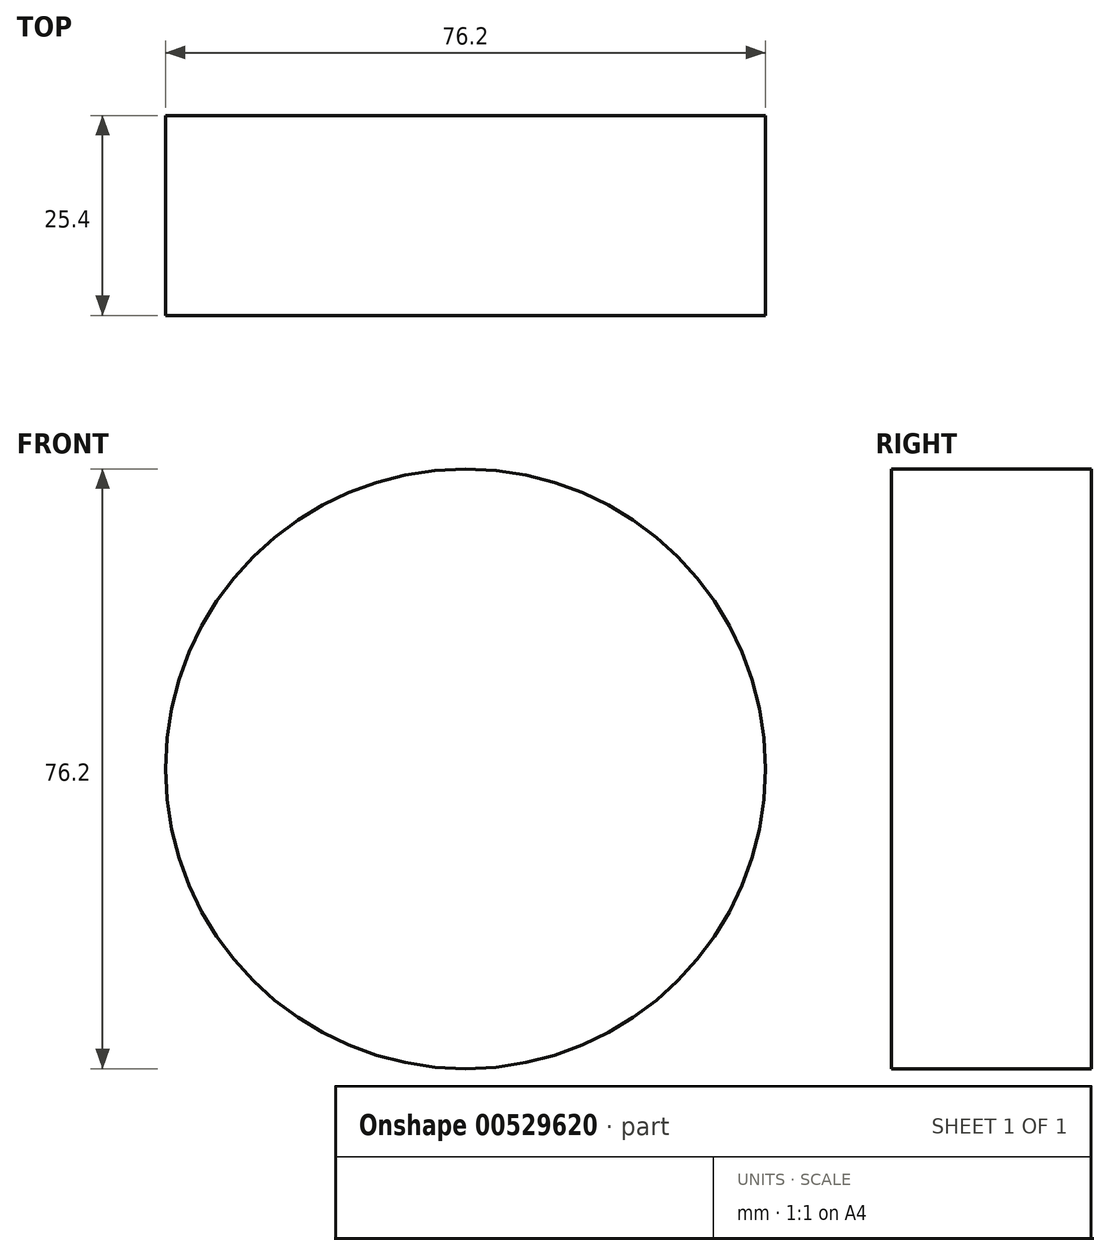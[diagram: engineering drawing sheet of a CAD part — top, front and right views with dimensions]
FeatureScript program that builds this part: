
annotation { "Feature Type Name" : "Feature", "Feature Type Description" : "" }
export const myFeature = defineFeature(function(context is Context, id is Id, definition is map)
    precondition{}
    {
        {
            var Q0;
            Q0=qCreatedBy(makeId("Front.planeOp"),FACE);
            var sketch = newSketch(context, id + "F0", { "sketchPlane" : qUnion([Q0])});
            skCircle(sketch, "E0", {"center": v(0, 0) * mm, "radius": 38.1 * mm});
            skSolve(sketch);
        }
        {
            var Q0;
            Q0 = qSketchRegion(id + "F0", true);
            extrude(context, id + "F1", {"entities" : qUnion([Q0]), "depth" : 25.4 * mm, "offsetDistance" : 25.4 * mm});
        }
    });
